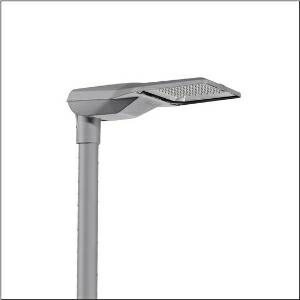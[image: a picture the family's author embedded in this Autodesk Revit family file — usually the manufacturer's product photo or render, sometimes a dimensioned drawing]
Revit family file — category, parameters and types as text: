
# Revit family: streetlight_sl_21_iq_midi___st1_0a_5xe3d41d08mb_7520
name_source: partatom
category: Lighting Fixtures
units: mm (PartAtom-declared; Revit-internal decimal feet)

## family parameters
Cut with Voids When Loaded = No
Host = Face
Light Source = No
Part Type = Normal
Room Calculation Point = No
Round Connector Dimension = Use Diameter
Shared = No

## types (1)
- --- (1 x LED, 20360 lm, 146.7 W, 4000K)
    Apparent Load = 147 VA
    CIE Flux Codes = 37 72 97 100 100
    Color Rendering = 70
    Color Temperature = 4000K
    Default Elevation = 1800 mm
    Description = Streetlight SL 21 iQ midi, mast luminaire, primary light control with lens, of PMMA, primary optical cover: cover, of toughened safety glass, transparent, light distribution: ST1.0a, light emission: direct distribution, primary light characteristic: asymmetric, installation type: post-top, side-entry, LED, High Power LED, rated luminous flux: 20.360lm, luminous efficacy: 139lm/W, light colour: 740, colour temperature: 4000K, control gear: iQ-Comfort, control: Auto-Match, Temp-Guard, Lumen-Switch, Night-Set, Smart-Wire, Light-Fading, Desk-Remote (wireless, voltage-free reading and setting of iQ features in the workshop via application-optimized NFC function/RFID function), optimised constant luminous flux control (CLO 2.0), pre-setting: linear dimming characteristic, mains connection: 230..240V, AC, 50/60Hz, start of lifetime: 147W, end of service life: 161W, reduction: 62W, luminaire housing, of diecast aluminium, powder-coated, Siteco® metallic grey (DB 702S), corrosivity category C5 mid according to DIN EN ISO 12944, please order mast flange separately, inclination adjustable: 0°, 5°, 10°, 15°, sealing non-destructively replaceable, multi-level sealing system, length: 644mm, width: 335mm, height: 110mm, mast flange for spigot size: 42mm (side-entry): 5XC10008XM4, 60/48mm (side-entry/post-top): 5XC10108XM2, 76/60mm (side-entry/post-top): 5XC10108XM1, mounting height: 4..8m, protection rating (complete): IP66, insulation class (complete): insulation class II (safety insulation), certification: CE, ENEC, ENEC+, VDE, impact resistance: IK10, permissible operating ambient temperature for outdoor applications: -40..+50°C, standard-compliant lighting for roads and squares, packaging unit: 1 piece

Light Distribution: ST1.0a
    Height = 111 mm
    Lamp = 1 x LED
    Lamp Light Flux = 20360 lm
    Lamp Power = 146.7 W
    Lamp count = 1
    Length = 644 mm
    Luminous efficacy = 139 lm/W
    Manufacturer = Siteco
    ModVariant = No
    Model = 5XE3D41D08MB
    Number of Poles = 1
    OnlyDefault = Yes
    Power Factor = 1
    Product Name = Streetlight SL 21 iQ midi | ST1.0a
    Product group = mast luminaire | pylon top
    ProductGroupID = 6100
    Protection Class = Protection class II
    Protection Degree = IP 66
    RLX_Detail_Level = 1
    RLX_Emergency_Light_Flux = 0 lm
    RLX_Emergency_Type = 0
    RLX_Emergency_Type_DB = No
    RlxData = <blob elided: 26881 chars, md5=c5809235>
    Socket = socket
    Standby Power = 0 W
    System Light Flux = 20360 lm
    System Power = 147 W
    Type Comments = factory setting: luminous flux: 100 % | dim-lin: 254 | 753 mA
    Type Image = l_1004298.jpg
    URL = http://relux.com
    VarID = @adj_189456
    Voltage = 0 V
    Weight = 0.00 kg
    Width = 336 mm

## geometry (parser evidence)
native form markers: Blend x4, Sweep x12
no freeform markers — native parametric forms only
